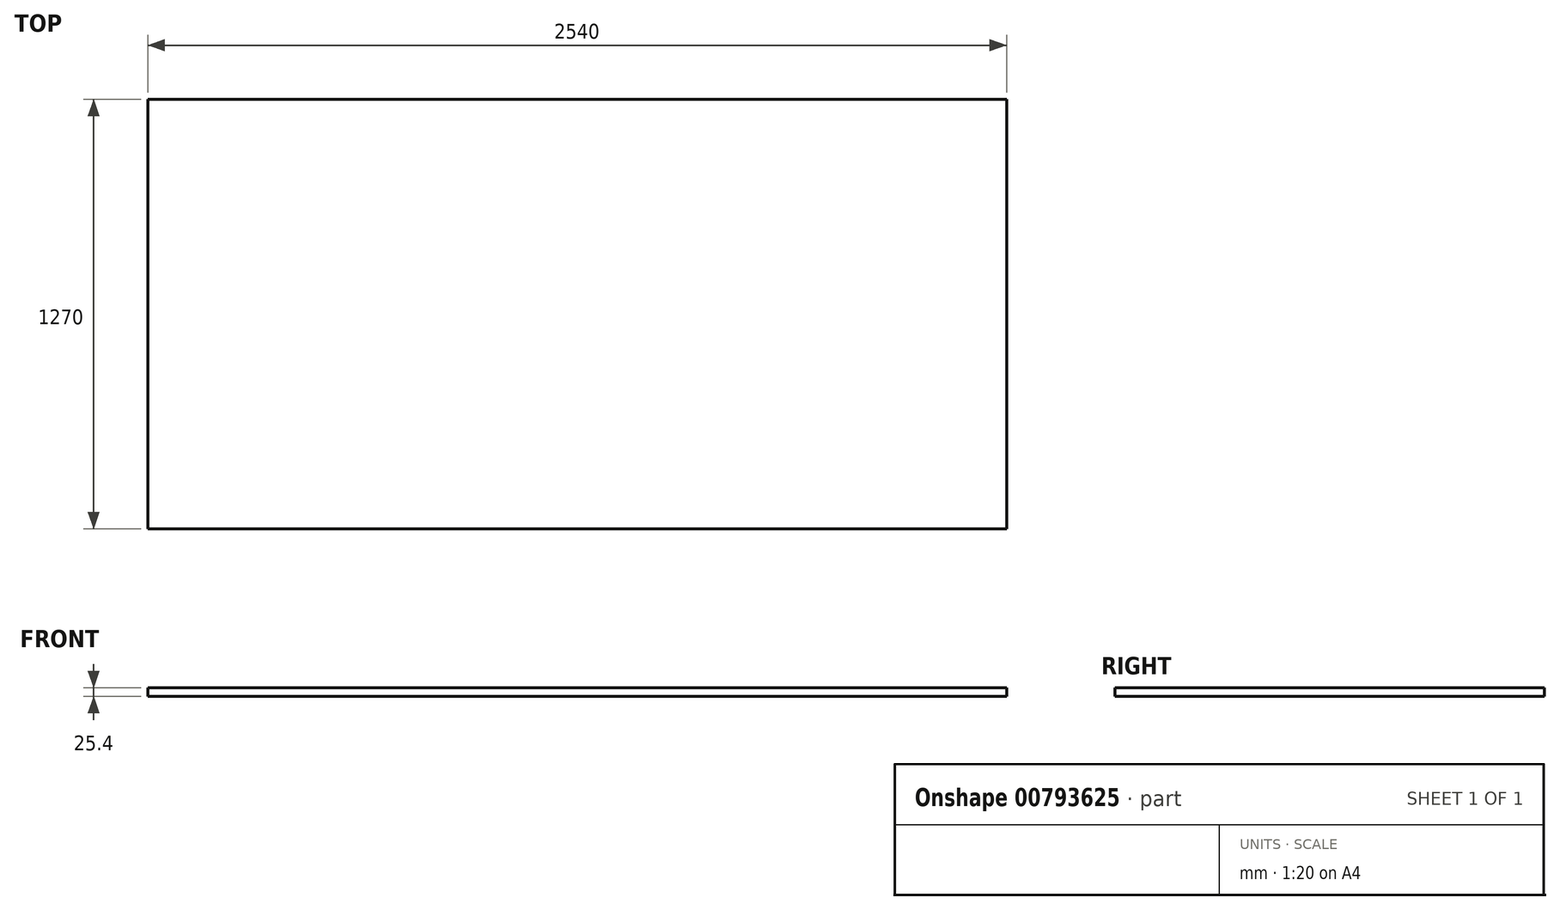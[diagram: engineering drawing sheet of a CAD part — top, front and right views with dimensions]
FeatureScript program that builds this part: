
annotation { "Feature Type Name" : "Feature", "Feature Type Description" : "" }
export const myFeature = defineFeature(function(context is Context, id is Id, definition is map)
    precondition{}
    {
        {
            var Q0;
            Q0=qCreatedBy(makeId("Top.planeOp"),FACE);
            var sketch = newSketch(context, id + "F0", { "sketchPlane" : qUnion([Q0])});
            skLineSegment(sketch, "E0.bottom", {"start": v(-1249.73, 498.78) * mm, "end": v(1290.27, 498.78) * mm});
            skLineSegment(sketch, "E0.top", {"start": v(-1249.73, -771.22) * mm, "end": v(1290.27, -771.22) * mm});
            skLineSegment(sketch, "E0.left", {"start": v(-1249.73, 498.78) * mm, "end": v(-1249.73, -771.22) * mm});
            skLineSegment(sketch, "E0.right", {"start": v(1290.27, 498.78) * mm, "end": v(1290.27, -771.22) * mm});
            skSolve(sketch);
        }
        {
            var Q0;
            Q0 = qSketchRegion(id + "F0", true);
            extrude(context, id + "F1", {"entities" : qUnion([Q0]), "depth" : 25.4 * mm, "offsetDistance" : 25.4 * mm});
        }
    });
